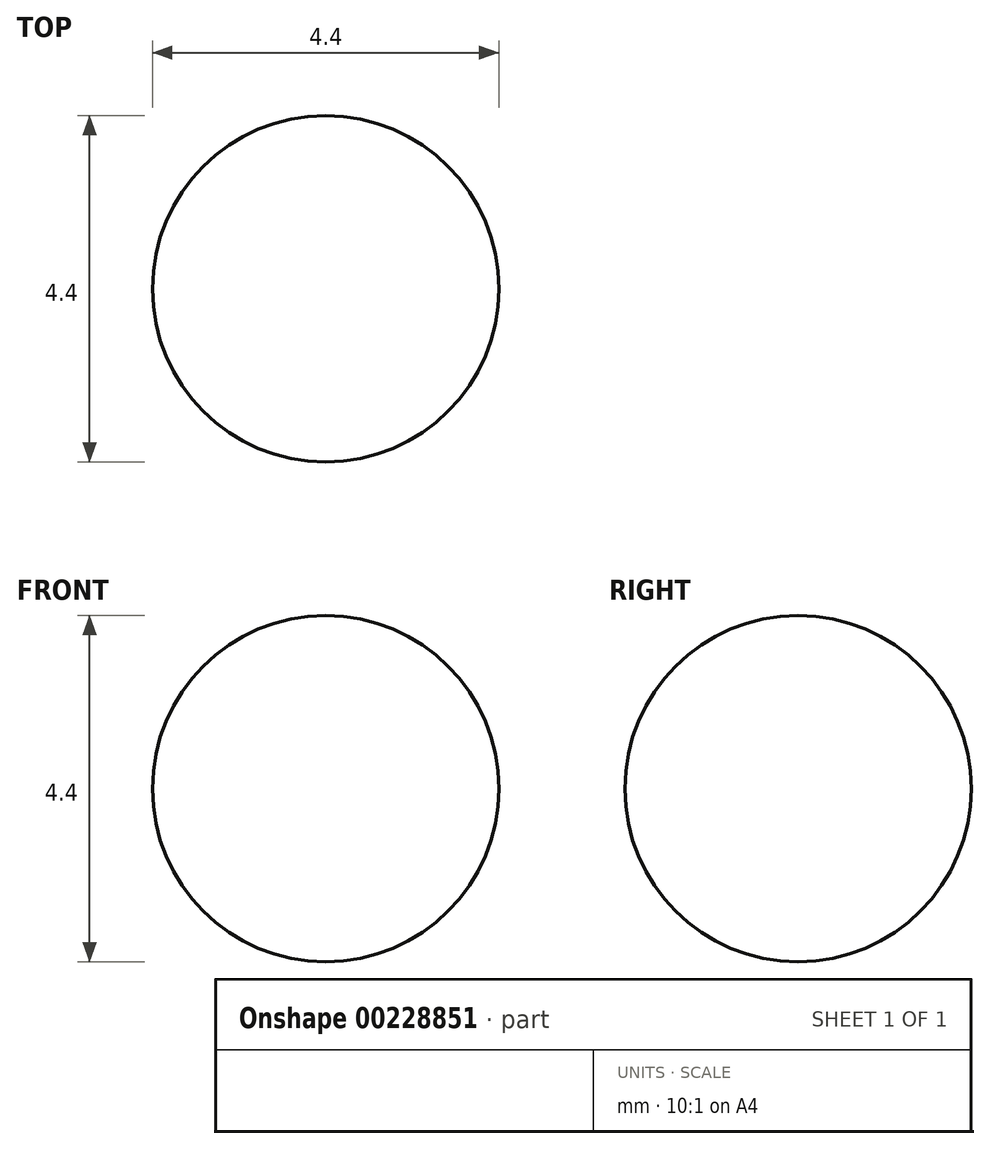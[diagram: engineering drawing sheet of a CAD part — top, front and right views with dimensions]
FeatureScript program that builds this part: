
annotation { "Feature Type Name" : "Feature", "Feature Type Description" : "" }
export const myFeature = defineFeature(function(context is Context, id is Id, definition is map)
    precondition{}
    {
        {
            var Q0;
            Q0=qCreatedBy(makeId("Front.planeOp"),FACE);
            var sketch = newSketch(context, id + "F0", { "sketchPlane" : qUnion([Q0])});
            skArc(sketch, "E0", {"start": v(0, 0) * mm, "mid": v(2.2, 2.2) * mm, "end": v(0, 4.4) * mm});
            skLineSegment(sketch, "E1", {"start": v(0, 4.4) * mm, "end": v(0, 0) * mm});
            skSolve(sketch);
        }
        {
            var Q0;
            Q0 = qSketchRegion(id + "F0", true);
            var Q1;
            Q1=sQuery(id+"F0.wireOp",EDGE,"E1");
            revolve(context, id + "F1", {"entities" : qUnion([Q0]), "axis" : qUnion([Q1]), "revolveType" : RevolveType.FULL});
        }
    });
